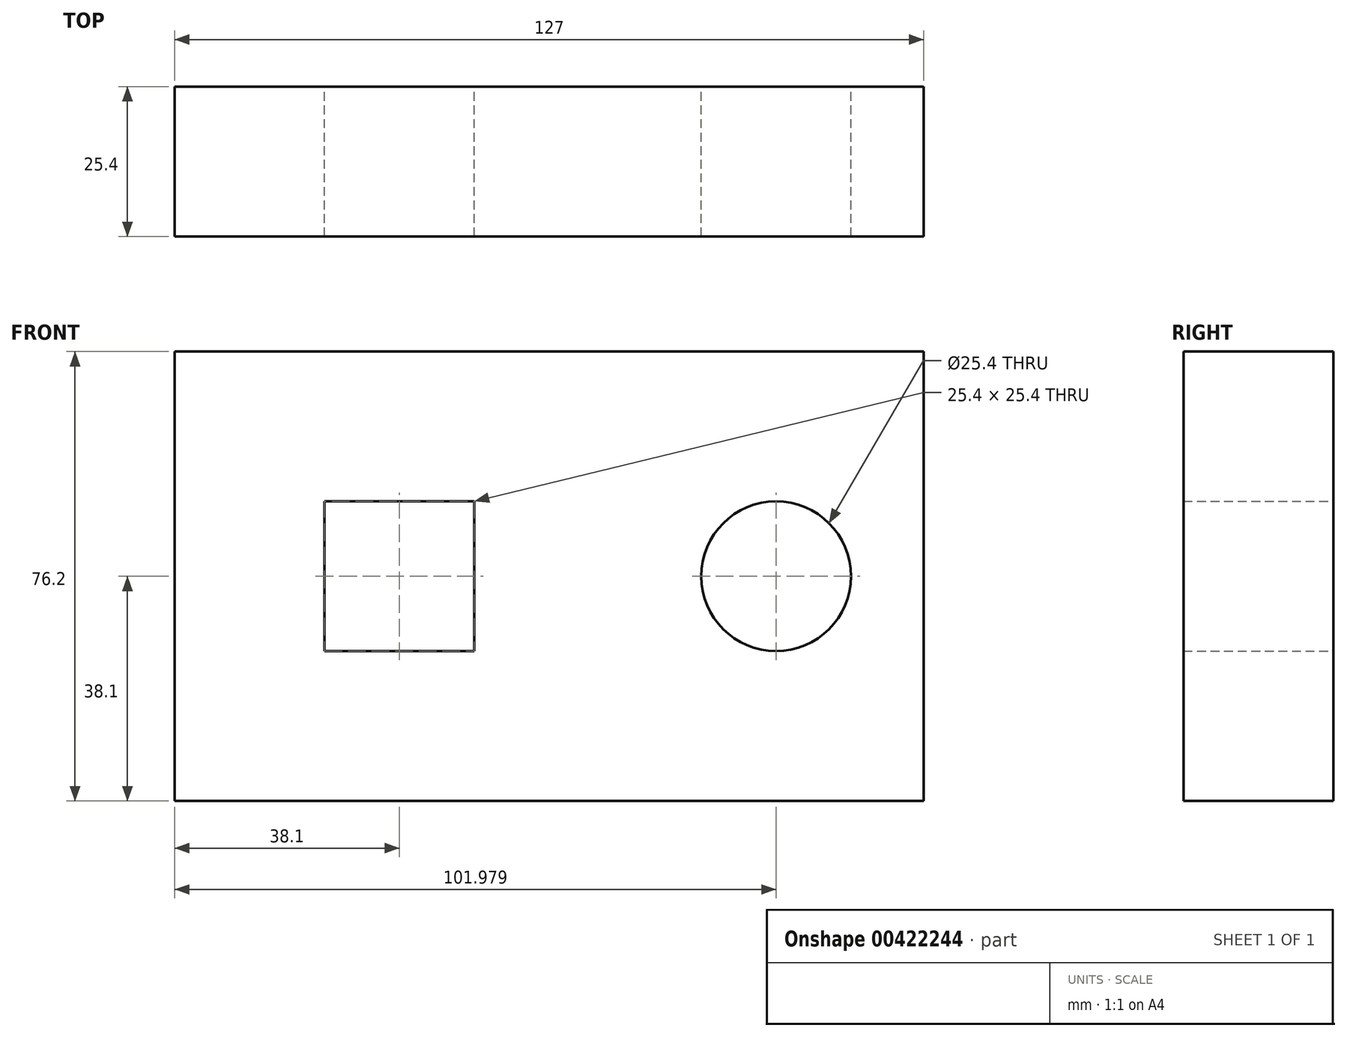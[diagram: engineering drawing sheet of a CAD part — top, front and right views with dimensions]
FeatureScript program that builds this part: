
annotation { "Feature Type Name" : "Feature", "Feature Type Description" : "" }
export const myFeature = defineFeature(function(context is Context, id is Id, definition is map)
    precondition{}
    {
        {
            var Q0;
            Q0=qCreatedBy(makeId("Front.planeOp"),FACE);
            var sketch = newSketch(context, id + "F0", { "sketchPlane" : qUnion([Q0])});
            skLineSegment(sketch, "E0.bottom", {"start": v(50.8, 0) * mm, "end": v(-76.2, 0) * mm});
            skLineSegment(sketch, "E0.top", {"start": v(50.8, 76.2) * mm, "end": v(-76.2, 76.2) * mm});
            skLineSegment(sketch, "E0.left", {"start": v(50.8, 0) * mm, "end": v(50.8, 76.2) * mm});
            skLineSegment(sketch, "E0.right", {"start": v(-76.2, 0) * mm, "end": v(-76.2, 76.2) * mm});
            skLineSegment(sketch, "E1.bottom", {"start": v(-50.8, 25.4) * mm, "end": v(-25.4, 25.4) * mm});
            skLineSegment(sketch, "E1.top", {"start": v(-50.8, 50.8) * mm, "end": v(-25.4, 50.8) * mm});
            skLineSegment(sketch, "E1.left", {"start": v(-50.8, 25.4) * mm, "end": v(-50.8, 50.8) * mm});
            skLineSegment(sketch, "E1.right", {"start": v(-25.4, 25.4) * mm, "end": v(-25.4, 50.8) * mm});
            skCircle(sketch, "E2", {"center": v(25.78, 38.1) * mm, "radius": 12.7 * mm});
            skSolve(sketch);
        }
        {
            var Q0;
            Q0 = qSketchRegion(id + "F0", true);
            extrude(context, id + "F1", {"entities" : qUnion([Q0]), "depth" : 25.4 * mm});
        }
    });
